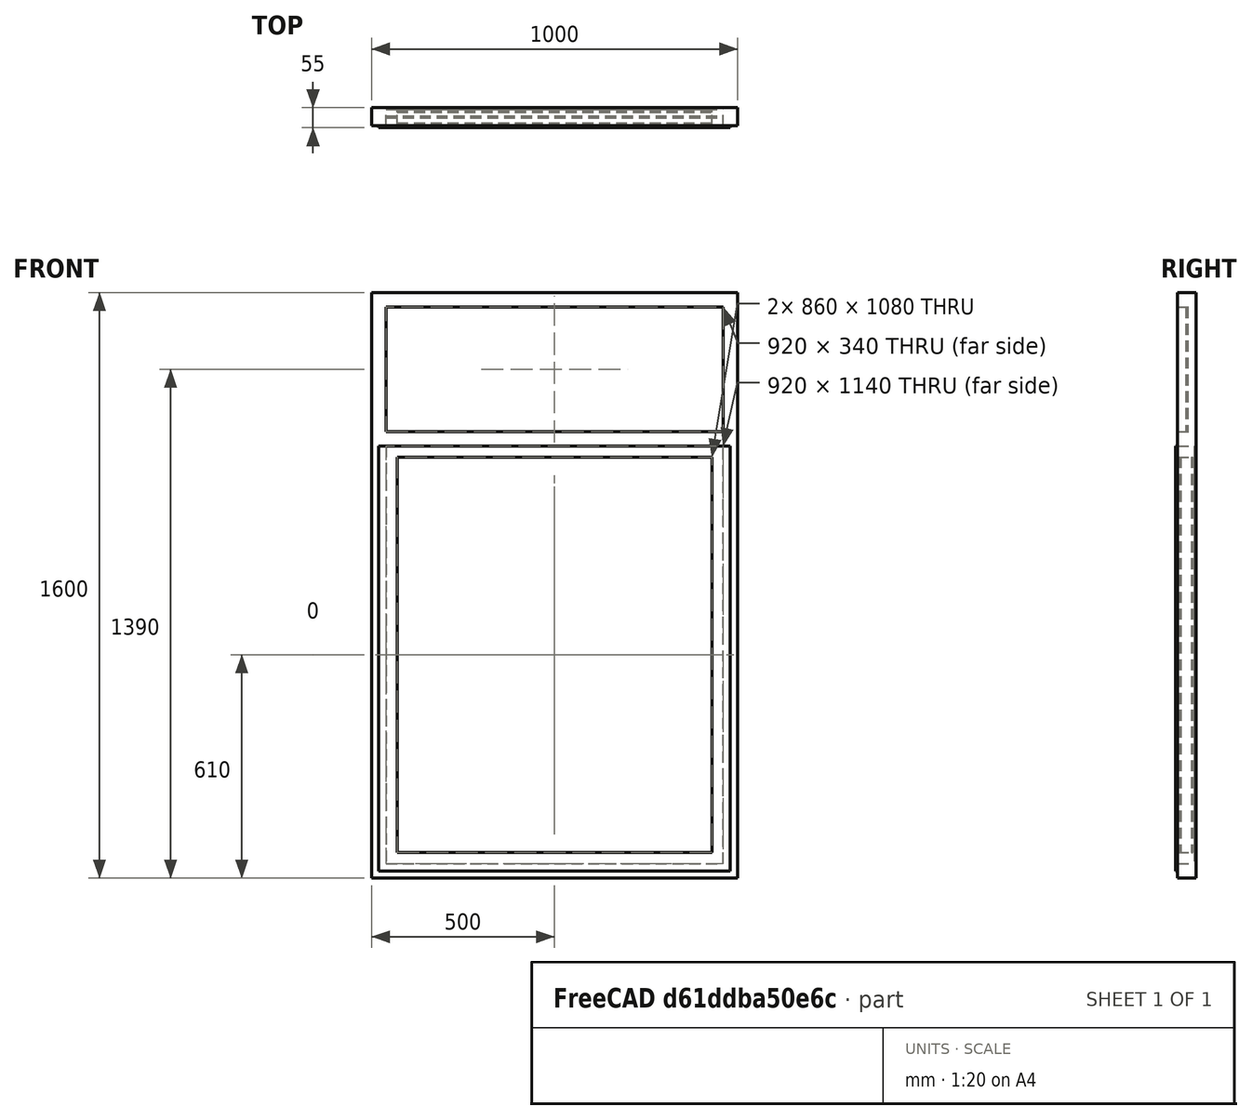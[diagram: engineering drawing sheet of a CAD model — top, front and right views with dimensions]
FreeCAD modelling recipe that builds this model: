
FCSTD DOCUMENT  (FreeCAD 0.16R6704 (Git))
Label: Maxim Air double fixed glass and bind
License: CreativeCommons Attribution
LicenseURL: http://creativecommons.org/licenses/by/4.0/
objects: Sketcher::SketchObject×3, Part::FeaturePython×2, Part::Extrusion×1, App::DocumentObjectGroup×1
note: 6 computed .brp shape members not serialized (recipe doc carries the construction recipe); baked Part::Feature solids carry a one-line shape summary decoded from their .brp

FEATURE [Sketcher::SketchObject] Sketch096  label="Esboco_persiana_01"
  Placement = pos=(0,0,0) rot=(1,0,0;1.5708rad)
  sketch-geometry (21):
    g0: LineSegment StartX=0 StartY=0 StartZ=0 EndX=1000 EndY=0 EndZ=0
    g1: LineSegment StartX=1000 StartY=0 StartZ=0 EndX=1000 EndY=1600 EndZ=0
    g2: LineSegment StartX=1000 StartY=1600 StartZ=0 EndX=0 EndY=1600 EndZ=0
    g3: LineSegment StartX=0 StartY=1600 StartZ=0 EndX=0 EndY=0 EndZ=0
    g4: LineSegment StartX=40 StartY=40 StartZ=0 EndX=960 EndY=40 EndZ=0
    g5: LineSegment StartX=960 StartY=40 StartZ=0 EndX=960 EndY=1180 EndZ=0
    g6: LineSegment StartX=960 StartY=1180 StartZ=0 EndX=40 EndY=1180 EndZ=0
    g7: LineSegment StartX=40 StartY=1180 StartZ=0 EndX=40 EndY=40 EndZ=0
    g8: LineSegment StartX=40 StartY=1560 StartZ=0 EndX=960 EndY=1560 EndZ=0
    g9: LineSegment StartX=960 StartY=1560 StartZ=0 EndX=960 EndY=1220 EndZ=0
    g10: LineSegment StartX=960 StartY=1220 StartZ=0 EndX=40 EndY=1220 EndZ=0
    g11: LineSegment StartX=40 StartY=1220 StartZ=0 EndX=40 EndY=1560 EndZ=0
    g12: LineSegment [constr] StartX=-307.315 StartY=1200 StartZ=0 EndX=1727 EndY=1200 EndZ=0
    g13: LineSegment StartX=70 StartY=1150 StartZ=0 EndX=930 EndY=1150 EndZ=0
    g14: LineSegment StartX=930 StartY=1150 StartZ=0 EndX=930 EndY=70 EndZ=0
    g15: LineSegment StartX=930 StartY=70 StartZ=0 EndX=70 EndY=70 EndZ=0
    g16: LineSegment StartX=70 StartY=70 StartZ=0 EndX=70 EndY=1150 EndZ=0
    g17: LineSegment StartX=20 StartY=1180 StartZ=0 EndX=980 EndY=1180 EndZ=0
    g18: LineSegment StartX=980 StartY=1180 StartZ=0 EndX=980 EndY=20 EndZ=0
    g19: LineSegment StartX=980 StartY=20 StartZ=0 EndX=20 EndY=20 EndZ=0
    g20: LineSegment StartX=20 StartY=20 StartZ=0 EndX=20 EndY=1180 EndZ=0
  constraints (61):
    c: Coincident(g0,g1)
    c: Coincident(g1,g2)
    c: Coincident(g2,g3)
    c: Coincident(g3,g0)
    c: Horizontal(g0)
    c: Horizontal(g2)
    c: Vertical(g1)
    c: Vertical(g3)
    c: Coincident(g4,g5)
    c: Coincident(g5,g6)
    c: Coincident(g6,g7)
    c: Coincident(g7,g4)
    c: Horizontal(g4)
    c: Horizontal(g6)
    c: Vertical(g5)
    c: Vertical(g7)
    c: DistanceX(g0) = 1000  'Largura_vao'
    c: DistanceX(g4,g0) = 40  'Largura_montante_vertical_2'
    c: DistanceY(g0,g4) = 40  'Altura_montante_inferior'
    c: Coincident(g0,g-1)
    c: Coincident(g8,g9)
    c: Coincident(g9,g10)
    c: Coincident(g10,g11)
    c: Coincident(g11,g8)
    c: Horizontal(g8)
    c: Horizontal(g10)
    c: Vertical(g9)
    c: Vertical(g11)
    c: DistanceX(g2,g8) = 40  'Largura_montante_vertical_1'
    c: DistanceY(g8,g2) = 40  'Montante_superior'
    c: DistanceY(g6,g10) = 40  'Altura_montante_inferior_bandeira'
    c: DistanceX(g9,g5) = 0
    c: Horizontal(g12)
    c: Symmetric(g9,g5,g12)
    c: DistanceY(g0,g1) = 1600  'Altura_vao'
    c: DistanceY(g0,g12) = 1200  'Altura_janela'
    c: Coincident(g13,g14)
    c: Coincident(g14,g15)
    c: Coincident(g15,g16)
    c: Coincident(g16,g13)
    c: Horizontal(g13)
    c: Horizontal(g15)
    c: Vertical(g14)
    c: Vertical(g16)
    c: DistanceX(g6,g13) = 30  'Largura_montante_vertical_1_janela'
    c: DistanceY(g13,g6) = 30  'Altura_montante_superior_janela'
    c: DistanceX(g13,g5) = 30  'Largura_montante_vertical_2_janela'
    c: DistanceY(g4,g14) = 30  'Altura_montante_inferior_janela'
    c: Coincident(g17,g18)
    c: Coincident(g18,g19)
    c: Coincident(g19,g20)
    c: Coincident(g20,g17)
    c: Horizontal(g17)
    c: Horizontal(g19)
    c: Vertical(g18)
    c: Vertical(g20)
    c: DistanceX(g4,g18) = 20  'Largura arremate vertical 2'
    c: DistanceY(g18,g4) = 20  'Altura arremate inferior'
    c: DistanceX(g19,g4) = 20  'Largura arremate 1 janela'
    c: DistanceY(g6,g17) = 0
    c: DistanceX(g10,g6) = 0
FEATURE [Part::FeaturePython] Window074  label="Maxim Air double fixed glass and bind "  # WARN: FeaturePython — macro-defined, semantics opaque (R4)
  Base = -> Sketch096
  Height = 1000
  HoleDepth = 0
  MoveWithHost = true
  Normal = (0,1,0)
  Preset = 1
  Role = 0
  Width = 1000
  WindowParts = CAIXILHO | Frame | Wire0,Wire1,Wire2 | 50.0 | 0.0 | JANELA | Frame | Wire1,Wire3 | 45.0 | 0.0 | VIDRO SUPERIOR | Glass panel | Wire2 | 5.0 | 22.5 | VIDRO 2 | Glass panel | Wire3 | 5.0 | 3.0 | VIDRO 3 | Glass panel | Wire3 | 5.0 | 37.0 | ARREMATE | Frame | Wire4,Wire3 | 5.0 | -5.0
FEATURE [Sketcher::SketchObject] Sketch097
  ExternalGeometry = -> [Window074]
  Placement = pos=(70,0,0) rot=(0.57735,0.57735,0.57735;2.0944rad)
  Support = -> Window074 [Face23]
  sketch-geometry (3):
    g0: ArcOfCircle CenterX=25 CenterY=1142 CenterZ=0 NormalX=0 NormalY=0 NormalZ=1 Radius=7 StartAngle=1.5708 EndAngle=4.71239
    g1: LineSegment [constr] StartX=25 StartY=1149.78 StartZ=0 EndX=25 EndY=-8819.31 EndZ=0
    g2: ArcOfCircle CenterX=25 CenterY=1128 CenterZ=0 NormalX=0 NormalY=0 NormalZ=1 Radius=7 StartAngle=4.71239 EndAngle=7.85398
  constraints (10):
    c: PointOnObject(g0,g1)
    c: PointOnObject(g0,g1)
    c: PointOnObject(g0,g1)
    c: Symmetric(g-4,g-4,g1)
    c: Coincident(g2,g0)
    c: PointOnObject(g2,g1)
    c: PointOnObject(g2,g1)
    c: DistanceY(g0,g-6) = 1
    c: DistanceY(g0,g0) = 14
    c: DistanceY(g2,g0) = 14
FEATURE [Part::Extrusion] Extrude_Sketch095  label="Módulo persiana001"
  Base = -> Sketch097
  Dir = (860,0,0)
  Solid = true
  expr: Dir.x = Esboco_persiana_01.Constraints.Largura_vao - Esboco_persiana_01.Constraints.Largura_montante_vertical_1 - Esboco_persiana_01.Constraints.Largura_montante_vertical_1_janela - Esboco_persiana_01.Constraints.Largura_montante_vertical_2_janela - Esboco_persiana_01.Constraints.Largura_montante_vertical_2
FEATURE [Part::FeaturePython] Array001  label="Internal blind "  # Draft array (typed FeaturePython)
  Angle = 360
  ArrayType = 0
  Axis = (0,0,1)
  Base = -> Extrude_Sketch095
  Center = (0,0,0)
  Fuse = false
  IntervalAxis = (0,0,0)
  IntervalX = (1,0,0)
  IntervalY = (0,1,0)
  IntervalZ = (0,0,-28)
  NumberPolar = 1
  NumberX = 1
  NumberY = 1
  NumberZ = 39
  expr: NumberZ = (Esboco_persiana_01.Constraints.Altura_janela - Esboco_persiana_01.Constraints.Altura_montante_inferior_bandeira / 2 - Esboco_persiana_01.Constraints.Altura_montante_superior_janela - Esboco_persiana_01.Constraints.Altura_montante_inferior_janela - Esboco_persiana_01.Constraints.Altura_montante_inferior) / 28
FEATURE [Sketcher::SketchObject] Sketch186  label="Opening indication"
  ExternalGeometry = -> [Window074]
  Placement = pos=(0,3,0) rot=(1,0,0;1.5708rad)
  Support = -> Window074 [Face35]
  sketch-geometry (3):
    g0: LineSegment StartX=70 StartY=1150 StartZ=0 EndX=500 EndY=70 EndZ=0
    g1: LineSegment StartX=500 StartY=70 StartZ=0 EndX=930 EndY=1150 EndZ=0
    g2: LineSegment [constr] StartX=500 StartY=1438 StartZ=0 EndX=500 EndY=-146 EndZ=0
  constraints (7):
    c: Coincident(g-4,g0)
    c: PointOnObject(g0,g-6)
    c: Coincident(g0,g1)
    c: Coincident(g1,g-5)
    c: Vertical(g2)
    c: Symmetric(g-6,g-6,g2)
    c: PointOnObject(g0,g2)
FEATURE [App::DocumentObjectGroup] Grupo082  label="Maxim Air double fixed glass and bind"
  Group = -> [Window074,Extrude_Sketch095,Array001,Sketch186]
